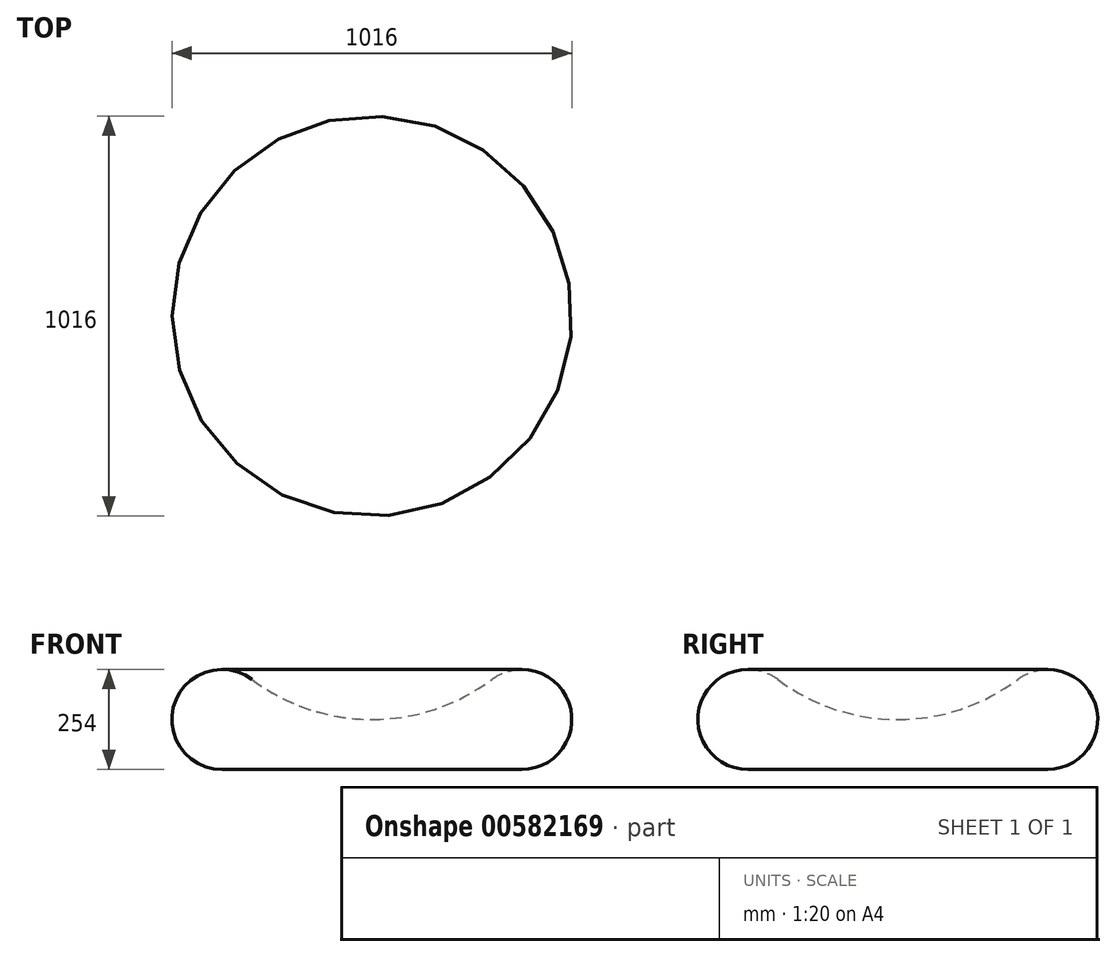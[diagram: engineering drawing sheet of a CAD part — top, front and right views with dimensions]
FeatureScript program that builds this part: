
annotation { "Feature Type Name" : "Feature", "Feature Type Description" : "" }
export const myFeature = defineFeature(function(context is Context, id is Id, definition is map)
    precondition{}
    {
        {
            var Q0;
            Q0=qCreatedBy(makeId("Front.planeOp"),FACE);
            var sketch = newSketch(context, id + "F0", { "sketchPlane" : qUnion([Q0])});
            skArc(sketch, "E0", {"start": v(-304.8, 326.38) * mm, "mid": v(-501.48, 264.94) * mm, "end": v(-381, 97.78) * mm});
            skArc(sketch, "E1", {"start": v(-304.8, 326.38) * mm, "mid": v(-160.64, 250.85) * mm, "end": v(0, 224.78) * mm});
            skLineSegment(sketch, "E2", {"start": v(-381, 97.78) * mm, "end": v(0, 97.78) * mm});
            skLineSegment(sketch, "E3", {"start": v(0, 97.78) * mm, "end": v(0, 224.78) * mm});
            skSolve(sketch);
        }
        {
            var Q0;
            Q0=makeQuery(id+"F0.imprint","IMPRINT",FACE,{"disambiguationData":[TD([[makeQuery(id+"F0.imprint","IMPRINT",EDGE,{"derivedFrom":sQuery(id+"F0.wireOp",EDGE,"E0")}),1.0]])]});
            var Q1;
            Q1=sQuery(id+"F0.wireOp",EDGE,"E3");
            revolve(context, id + "F1", {"entities" : qUnion([Q0]), "axis" : qUnion([Q1]), "revolveType" : RevolveType.FULL});
        }
        {
            var Q0;
            Q0=qCreatedBy(makeId("Top.planeOp"),FACE);
            cPlane(context, id + "F2", {"entities" : qUnion([Q0]), "cplaneType" : CPlaneType.OFFSET, "offset" : 497.84 * mm, "width" : 152.4 * mm, "height" : 152.4 * mm});
        }
    });
